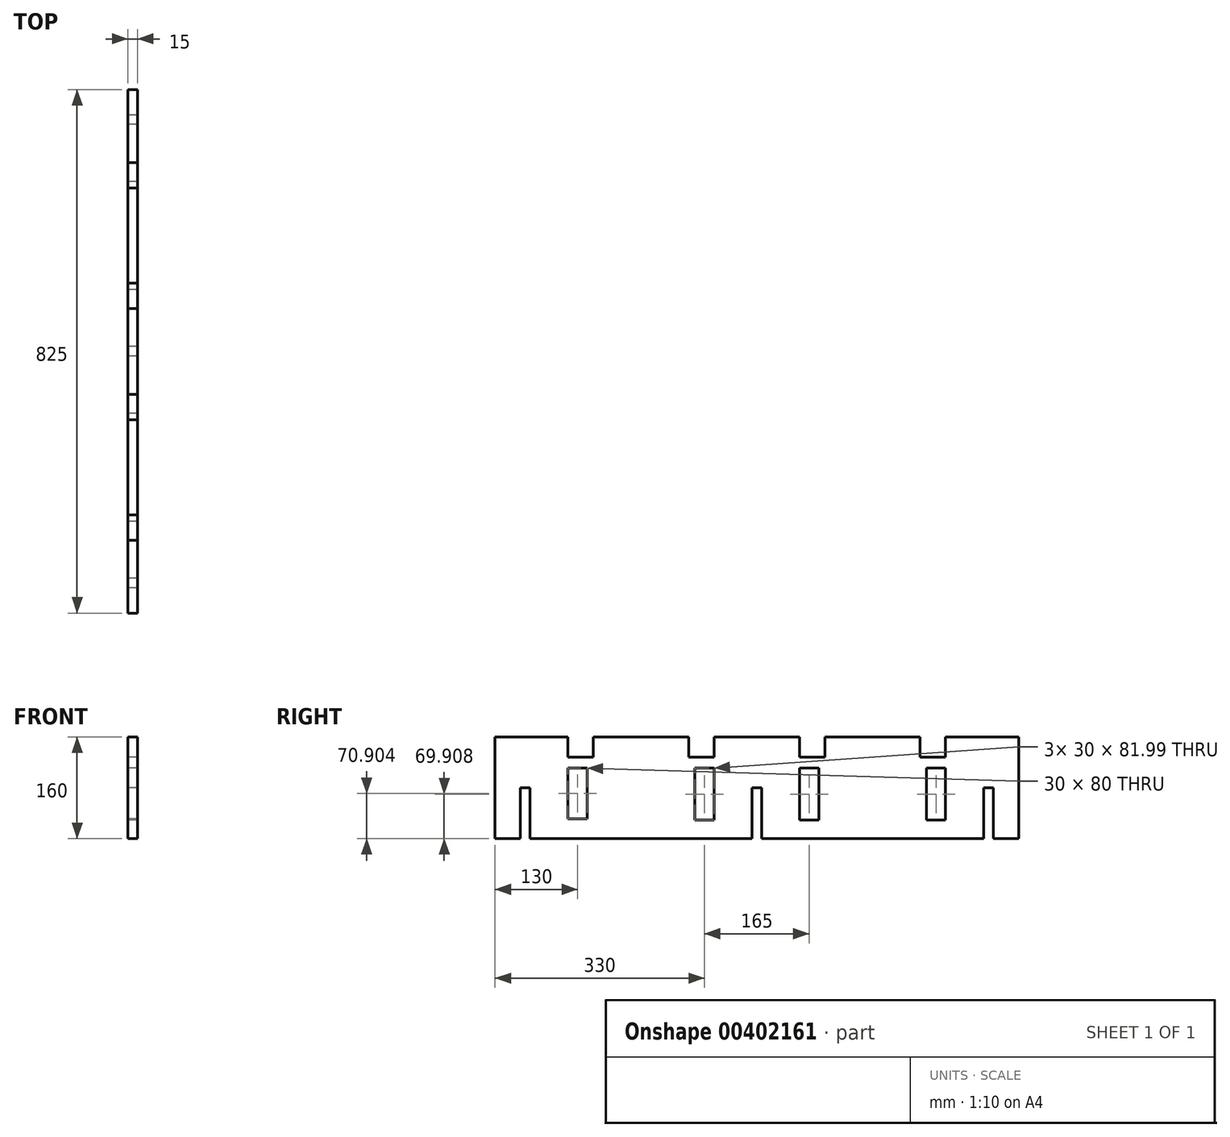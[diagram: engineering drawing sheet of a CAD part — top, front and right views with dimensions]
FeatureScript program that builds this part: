
annotation { "Feature Type Name" : "Feature", "Feature Type Description" : "" }
export const myFeature = defineFeature(function(context is Context, id is Id, definition is map)
    precondition{}
    {
        {
            var Q0;
            Q0=qCreatedBy(makeId("Right.planeOp"),FACE);
            var sketch = newSketch(context, id + "F0", { "sketchPlane" : qUnion([Q0])});
            skLineSegment(sketch, "E0.bottom", {"start": v(-412.5, 80) * mm, "end": v(-297.5, 80) * mm});
            skLineSegment(sketch, "E0.top", {"start": v(-412.5, -80) * mm, "end": v(-372.5, -80) * mm});
            skLineSegment(sketch, "E0.left", {"start": v(-412.5, 80) * mm, "end": v(-412.5, -80) * mm});
            skLineSegment(sketch, "E0.right", {"start": v(412.5, 80) * mm, "end": v(412.5, -80) * mm});
            skLineSegment(sketch, "E1", {"start": v(-372.5, -80) * mm, "end": v(-372.5, 0) * mm});
            skLineSegment(sketch, "E2", {"start": v(-372.5, 0) * mm, "end": v(-357.5, 0) * mm});
            skLineSegment(sketch, "E3", {"start": v(-357.5, 0) * mm, "end": v(-357.5, -80) * mm});
            skLineSegment(sketch, "E4", {"start": v(-7.5, -80) * mm, "end": v(-7.5, 0) * mm});
            skLineSegment(sketch, "E5", {"start": v(-7.5, 0) * mm, "end": v(7.5, 0) * mm});
            skLineSegment(sketch, "E6", {"start": v(7.5, 0) * mm, "end": v(7.5, -80) * mm});
            skLineSegment(sketch, "E7", {"start": v(357.5, -80) * mm, "end": v(357.5, 0) * mm});
            skLineSegment(sketch, "E8", {"start": v(357.5, 0) * mm, "end": v(372.5, 0) * mm});
            skLineSegment(sketch, "E9", {"start": v(372.5, 0) * mm, "end": v(372.5, -80) * mm});
            skLineSegment(sketch, "E10.trimOffspring", {"start": v(372.5, -80) * mm, "end": v(412.5, -80) * mm});
            skLineSegment(sketch, "E11", {"start": v(-357.5, -80) * mm, "end": v(-7.5, -80) * mm});
            skLineSegment(sketch, "E12", {"start": v(7.5, -80) * mm, "end": v(357.5, -80) * mm});
            skLineSegment(sketch, "E13", {"start": v(-297.5, 80) * mm, "end": v(-297.5, 48) * mm});
            skLineSegment(sketch, "E14", {"start": v(-297.5, 48) * mm, "end": v(-257.5, 48) * mm});
            skLineSegment(sketch, "E15", {"start": v(-257.5, 48) * mm, "end": v(-257.5, 80) * mm});
            skLineSegment(sketch, "E16", {"start": v(-257.5, 80) * mm, "end": v(-107.5, 80) * mm});
            skLineSegment(sketch, "E17", {"start": v(-107.5, 80) * mm, "end": v(-107.5, 48) * mm});
            skLineSegment(sketch, "E18", {"start": v(-107.5, 48) * mm, "end": v(-67.5, 48) * mm});
            skLineSegment(sketch, "E19", {"start": v(-67.5, 48) * mm, "end": v(-67.5, 80) * mm});
            skLineSegment(sketch, "E20", {"start": v(-67.5, 80) * mm, "end": v(67.5, 80) * mm});
            skLineSegment(sketch, "E21", {"start": v(67.5, 80) * mm, "end": v(67.5, 48) * mm});
            skLineSegment(sketch, "E22", {"start": v(67.5, 48) * mm, "end": v(107.5, 48) * mm});
            skLineSegment(sketch, "E23", {"start": v(107.5, 48) * mm, "end": v(107.5, 80) * mm});
            skLineSegment(sketch, "E24", {"start": v(107.5, 80) * mm, "end": v(257.5, 80) * mm});
            skLineSegment(sketch, "E25", {"start": v(257.5, 80) * mm, "end": v(257.5, 48) * mm});
            skLineSegment(sketch, "E26", {"start": v(257.5, 48) * mm, "end": v(297.5, 48) * mm});
            skLineSegment(sketch, "E27", {"start": v(297.5, 48) * mm, "end": v(297.5, 80) * mm});
            skLineSegment(sketch, "E28.trimOffspring", {"start": v(297.5, 80) * mm, "end": v(412.5, 80) * mm});
            skLineSegment(sketch, "E29.bottom", {"start": v(-297.5, 30.9) * mm, "end": v(-267.5, 30.9) * mm});
            skLineSegment(sketch, "E29.top", {"start": v(-297.5, -49.1) * mm, "end": v(-267.5, -49.1) * mm});
            skLineSegment(sketch, "E29.left", {"start": v(-297.5, 30.9) * mm, "end": v(-297.5, -49.1) * mm});
            skLineSegment(sketch, "E29.right", {"start": v(-267.5, 30.9) * mm, "end": v(-267.5, -49.1) * mm});
            skLineSegment(sketch, "E30.bottom", {"start": v(-67.5, 30.9) * mm, "end": v(-97.5, 30.9) * mm});
            skLineSegment(sketch, "E30.top", {"start": v(-67.5, -51.09) * mm, "end": v(-97.5, -51.09) * mm});
            skLineSegment(sketch, "E30.left", {"start": v(-67.5, 30.9) * mm, "end": v(-67.5, -51.09) * mm});
            skLineSegment(sketch, "E30.right", {"start": v(-97.5, 30.9) * mm, "end": v(-97.5, -51.09) * mm});
            skLineSegment(sketch, "E31.bottom", {"start": v(67.5, 30.9) * mm, "end": v(97.5, 30.9) * mm});
            skLineSegment(sketch, "E31.top", {"start": v(67.5, -51.09) * mm, "end": v(97.5, -51.09) * mm});
            skLineSegment(sketch, "E31.left", {"start": v(67.5, 30.9) * mm, "end": v(67.5, -51.09) * mm});
            skLineSegment(sketch, "E31.right", {"start": v(97.5, 30.9) * mm, "end": v(97.5, -51.09) * mm});
            skLineSegment(sketch, "E32.bottom", {"start": v(297.5, 30.9) * mm, "end": v(267.5, 30.9) * mm});
            skLineSegment(sketch, "E32.top", {"start": v(297.5, -51.09) * mm, "end": v(267.5, -51.09) * mm});
            skLineSegment(sketch, "E32.left", {"start": v(297.5, 30.9) * mm, "end": v(297.5, -51.09) * mm});
            skLineSegment(sketch, "E32.right", {"start": v(267.5, 30.9) * mm, "end": v(267.5, -51.09) * mm});
            skLineSegment(sketch, "E33", {"start": v(-357.5, -80) * mm, "end": v(-332.5, -80) * mm});
            skLineSegment(sketch, "E34", {"start": v(357.5, -80) * mm, "end": v(332.5, -80) * mm});
            skSolve(sketch);
        }
        {
            var Q0;
            Q0 = qSketchRegion(id + "F0", true);
            extrude(context, id + "F1", {"entities" : qUnion([Q0]), "depth" : 15 * mm});
        }
    });
